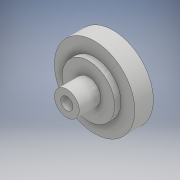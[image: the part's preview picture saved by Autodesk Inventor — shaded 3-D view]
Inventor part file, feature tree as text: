
AUTODESK INVENTOR PART (.ipt)
format: ipt  version: 2017 (Build 210142000, 142)  size: 300,032 bytes
history: native  units: mm
features: sketch x6, extrude x5, hole x1, pattern_circular x1, chamfer x1
ambient origin geometry x8: Origin, YZ Plane, XZ Plane, XY Plane, X Axis, Y Axis, Z Axis, Center Point
bodies: Solid1 (feature_tree)
feature tree (14):
  extrude  "Extrusion1"  Depth=2.0mm TaperAngle=0.0deg
  extrude  "Extrusion2"  Depth=6.0mm TaperAngle=0.0deg
  extrude  "Extrusion3"  Depth=7.0mm TaperAngle=0.0deg
  hole  "Hole1"  [1 undecoded]
  extrude  "Extrusion5"  Depth=10.0mm TaperAngle=0.0deg
  extrude  "Extrusion6"  Depth=2.0mm TaperAngle=360.0deg
  pattern_circular  "Circular Pattern1"  Angle=45.0deg  [1 undecoded]
  chamfer  "Chamfer2"  [1 undecoded]
  sketch  "Sketch1"  dims[d0=17.0mm d1=2.0mm d2=0.0mm]
  sketch  "Sketch2"  dims[d3=26.0mm d4=6.0mm d5=0.0mm]
  sketch  "Sketch3"  dims[d6=8.0mm d7=7.0mm d8=0.0mm]
  sketch  "Sketch4"  dims[d9=3.9mm d10=6.0mm d11=4.0mm d12=2.0mm d13=90.0deg d14=10.0mm d15=20.594885mm d24=1.8mm]
  sketch  "Sketch6"  dims[d25=10.0mm d26=5.0mm d27=0.0mm]
  sketch  "Sketch7"  dims[d30=5.0mm d31=0.0mm d32=200.0mm d33=360.0deg d35=2.0mm d36=2.0mm d37=45.0deg]
note: 3 required parameter values undecoded (feature->parameter linkage not recoverable at this tier; creation-order binding heuristic only, values carry confidence <= 0.55)
